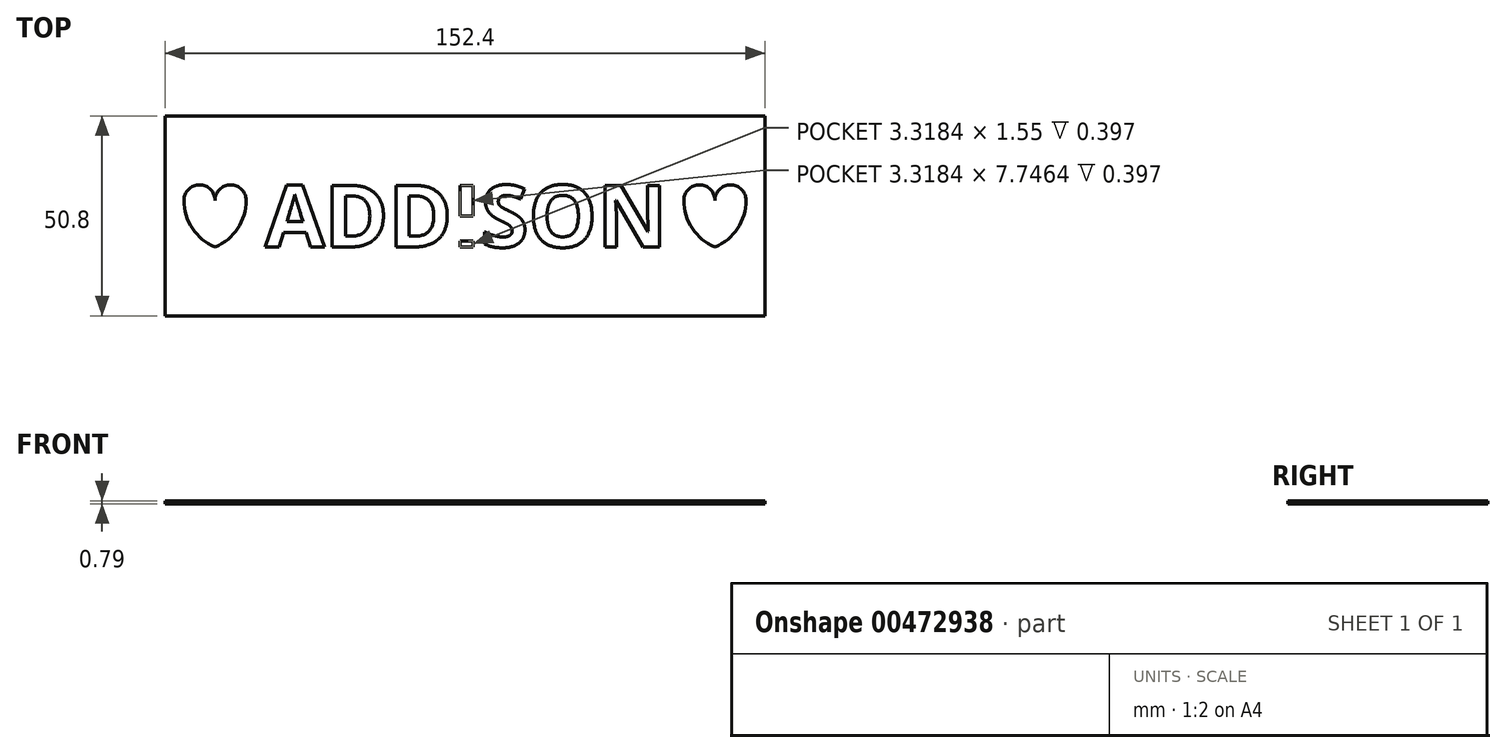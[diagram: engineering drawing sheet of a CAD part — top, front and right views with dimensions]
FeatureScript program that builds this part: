
annotation { "Feature Type Name" : "Feature", "Feature Type Description" : "" }
export const myFeature = defineFeature(function(context is Context, id is Id, definition is map)
    precondition{}
    {
        {
            var Q0;
            Q0=qCreatedBy(makeId("Top.planeOp"),FACE);
            var sketch = newSketch(context, id + "F0", { "sketchPlane" : qUnion([Q0])});
            skLineSegment(sketch, "E0", {"start": v(0, 0) * mm, "end": v(0, 25.4) * mm});
            skLineSegment(sketch, "E1", {"start": v(0, 25.4) * mm, "end": v(-76.2, 25.4) * mm});
            skLineSegment(sketch, "E2", {"start": v(-76.2, 25.4) * mm, "end": v(-76.2, -25.4) * mm});
            skLineSegment(sketch, "E3", {"start": v(-76.2, -25.4) * mm, "end": v(76.2, -25.4) * mm});
            skLineSegment(sketch, "E4", {"start": v(76.2, -25.4) * mm, "end": v(76.2, 25.4) * mm});
            skLineSegment(sketch, "E5", {"start": v(76.2, 25.4) * mm, "end": v(0, 25.4) * mm});
            skSolve(sketch);
        }
        {
            var Q0;
            Q0 = qSketchRegion(id + "F0", true);
            extrude(context, id + "F1", {"entities" : qUnion([Q0]), "depth" : 0.8 * mm, "offsetDistance" : 25.4 * mm});
        }
        {
            var Q0;
            Q0=makeQuery(id+"F1.opExtrude","CAP_FACE",FACE,{"disambiguationData":[OSD([sQuery(id+"F0.wireOp",EDGE,"E1"),sQuery(id+"F0.wireOp",EDGE,"E2"),sQuery(id+"F0.wireOp",EDGE,"E3"),sQuery(id+"F0.wireOp",EDGE,"E4"),sQuery(id+"F0.wireOp",EDGE,"E5")])],"isStart":false});
            var sketch = newSketch(context, id + "F2", { "sketchPlane" : qUnion([Q0])});
            skLineSegment(sketch, "E6.top", {"start": v(-44.45, -6.35) * mm, "end": v(44.45, -6.35) * mm});
            skPoint(sketch, "E6.middle", {"position": v(0, 0) * mm});
            skText(sketch, "E7", { "text": "ADDISON", "fontName": "OpenSans-Bold.ttf"});
            skLineSegment(sketch, "E8", {"start": v(0, 0) * mm, "end": v(-63.5, 0) * mm});
            skPoint(sketch, "E8.endSnap0", {"position": v(-76.2, 0) * mm});
            skLineSegment(sketch, "E9", {"start": v(-63.5, 0) * mm, "end": v(63.5, 0) * mm});
            skLineSegment(sketch, "E10", {"start": v(-63.5, 0) * mm, "end": v(-63.5, -7.9) * mm});
            skLineSegment(sketch, "E11", {"start": v(-63.5, 0) * mm, "end": v(-63.5, 3.94) * mm});
            skLineSegment(sketch, "E12", {"start": v(-63.5, 3.94) * mm, "end": v(-59.56, 3.94) * mm});
            skLineSegment(sketch, "E13", {"start": v(-63.5, 3.94) * mm, "end": v(-67.44, 3.94) * mm});
            skArc(sketch, "E14", {"start": v(-55.61, 3.94) * mm, "mid": v(-59.56, 7.89) * mm, "end": v(-63.5, 3.94) * mm});
            skArc(sketch, "E15", {"start": v(-63.5, 3.94) * mm, "mid": v(-67.44, 7.89) * mm, "end": v(-71.39, 3.94) * mm});
            skArc(sketch, "E16", {"start": v(-63.5, -7.9) * mm, "mid": v(-57.74, -3.18) * mm, "end": v(-55.61, 3.94) * mm});
            skArc(sketch, "E17", {"start": v(-71.39, 3.94) * mm, "mid": v(-69.26, -3.18) * mm, "end": v(-63.5, -7.9) * mm});
            skLineSegment(sketch, "E18", {"start": v(63.5, 0) * mm, "end": v(63.5, -7.9) * mm});
            skLineSegment(sketch, "E19", {"start": v(63.5, 0) * mm, "end": v(63.5, 3.94) * mm});
            skLineSegment(sketch, "E20", {"start": v(63.5, 3.94) * mm, "end": v(59.56, 3.94) * mm});
            skLineSegment(sketch, "E21", {"start": v(63.5, 3.94) * mm, "end": v(67.44, 3.94) * mm});
            skArc(sketch, "E22", {"start": v(63.5, 3.94) * mm, "mid": v(59.56, 7.89) * mm, "end": v(55.61, 3.94) * mm});
            skArc(sketch, "E23", {"start": v(71.39, 3.94) * mm, "mid": v(67.44, 7.89) * mm, "end": v(63.5, 3.94) * mm});
            skArc(sketch, "E24", {"start": v(63.5, -7.9) * mm, "mid": v(69.26, -3.18) * mm, "end": v(71.39, 3.94) * mm});
            skArc(sketch, "E25", {"start": v(55.61, 3.94) * mm, "mid": v(57.74, -3.18) * mm, "end": v(63.5, -7.9) * mm});
            const initialGuessF2  = {"E7": [-0.0508, -0.0079, 1, 0, 0.01578]};
            skSetInitialGuess(sketch, initialGuessF2);
            skSolve(sketch);
        }
        {
            var Q0;
            {var subQ6=sQuery(id+"F2.wireOp",EDGE,"E7.sketch_text.stroke-84");Q0=makeQuery(id+"F2.imprint","IMPRINT",FACE,{"disambiguationData":[TD([[makeQuery(id+"F2.imprint","IMPRINT",EDGE,{"derivedFrom":subQ6}),-1.0]])]});}
            var Q1;
            {var subQ4=sQuery(id+"F2.wireOp",EDGE,"E7.sketch_text.stroke-82");Q1=makeQuery(id+"F2.imprint","IMPRINT",FACE,{"disambiguationData":[TD([[makeQuery(id+"F2.imprint","IMPRINT",EDGE,{"derivedFrom":subQ4}),-1.0]])]});}
            var Q2;
            {var subQ4=sQuery(id+"F2.wireOp",EDGE,"E7.sketch_text.stroke-93");Q2=makeQuery(id+"F2.imprint","IMPRINT",FACE,{"disambiguationData":[TD([[makeQuery(id+"F2.imprint","IMPRINT",EDGE,{"derivedFrom":subQ4}),-1.0]])]});}
            var Q3;
            {var subQ3=sQuery(id+"F2.wireOp",EDGE,"E6.top");var subQ5=sQuery(id+"F2.wireOp",EDGE,"E7.sketch_text.stroke-88");var subQ6=makeQuery(id+"F2.imprint","INTERSECT",VERTEX,{"derivedFrom":[subQ3,subQ5]});Q3=makeQuery(id+"F2.imprint","IMPRINT",FACE,{"disambiguationData":[TD([[makeQuery(id+"F2.imprint","IMPRINT",EDGE,{"disambiguationData":[TD([[subQ6,-1.0]])],"derivedFrom":subQ3}),1.0]])]});}
            var Q4;
            {var subQ5=sQuery(id+"F2.wireOp",EDGE,"E7.sketch_text.stroke-87");Q4=makeQuery(id+"F2.imprint","IMPRINT",FACE,{"disambiguationData":[TD([[makeQuery(id+"F2.imprint","IMPRINT",EDGE,{"derivedFrom":subQ5}),-1.0]])]});}
            var Q5;
            {var subQ6=sQuery(id+"F2.wireOp",EDGE,"E7.sketch_text.stroke-68");Q5=makeQuery(id+"F2.imprint","IMPRINT",FACE,{"disambiguationData":[TD([[makeQuery(id+"F2.imprint","IMPRINT",EDGE,{"derivedFrom":subQ6}),-1.0]])]});}
            var Q6;
            {var subQ4=sQuery(id+"F2.wireOp",EDGE,"E7.sketch_text.stroke-73");Q6=makeQuery(id+"F2.imprint","IMPRINT",FACE,{"disambiguationData":[TD([[makeQuery(id+"F2.imprint","IMPRINT",EDGE,{"derivedFrom":subQ4}),-1.0]])]});}
            var Q7;
            {var subQ0=sQuery(id+"F2.wireOp",EDGE,"E7.sketch_text.stroke-70");var subQ1=sQuery(id+"F2.wireOp",EDGE,"E6.top");var subQ2=makeQuery(id+"F2.imprint","INTERSECT",VERTEX,{"derivedFrom":[subQ1,subQ0]});Q7=makeQuery(id+"F2.imprint","IMPRINT",FACE,{"disambiguationData":[TD([[makeQuery(id+"F2.imprint","IMPRINT",EDGE,{"disambiguationData":[TD([[subQ2,-1.0]])],"derivedFrom":subQ1}),-1.0]])]});}
            var Q8;
            {var subQ10=sQuery(id+"F2.wireOp",EDGE,"E7.sketch_text.stroke-44");Q8=makeQuery(id+"F2.imprint","IMPRINT",FACE,{"disambiguationData":[TD([[makeQuery(id+"F2.imprint","IMPRINT",EDGE,{"derivedFrom":subQ10}),-1.0]])]});}
            var Q9;
            {var subQ5=sQuery(id+"F2.wireOp",EDGE,"E7.sketch_text.stroke-52");Q9=makeQuery(id+"F2.imprint","IMPRINT",FACE,{"disambiguationData":[TD([[makeQuery(id+"F2.imprint","IMPRINT",EDGE,{"derivedFrom":subQ5}),-1.0]])]});}
            var Q10;
            {var subQ1=sQuery(id+"F2.wireOp",EDGE,"E7.sketch_text.stroke-41");Q10=makeQuery(id+"F2.imprint","IMPRINT",FACE,{"disambiguationData":[TD([[makeQuery(id+"F2.imprint","IMPRINT",EDGE,{"derivedFrom":subQ1}),-1.0]])]});}
            var Q11;
            {var subQ5=sQuery(id+"F2.wireOp",EDGE,"E7.sketch_text.stroke-39");Q11=makeQuery(id+"F2.imprint","IMPRINT",FACE,{"disambiguationData":[TD([[makeQuery(id+"F2.imprint","IMPRINT",EDGE,{"derivedFrom":subQ5}),-1.0]])]});}
            var Q12;
            {var subQ3=sQuery(id+"F2.wireOp",EDGE,"E9");var subQ5=makeQuery(id+"F2.imprint","IMPRINT",VERTEX,{"derivedFrom":subQ3});Q12=makeQuery(id+"F2.imprint","IMPRINT",FACE,{"disambiguationData":[TD([[makeQuery(id+"F2.imprint","IMPRINT",EDGE,{"disambiguationData":[TD([[subQ5,1.0]])],"derivedFrom":subQ3}),-1.0]])]});}
            var Q13;
            {var subQ5=sQuery(id+"F2.wireOp",EDGE,"E7.sketch_text.stroke-37");Q13=makeQuery(id+"F2.imprint","IMPRINT",FACE,{"disambiguationData":[TD([[makeQuery(id+"F2.imprint","IMPRINT",EDGE,{"derivedFrom":subQ5}),-1.0]])]});}
            var Q14;
            {var subQ0=sQuery(id+"F2.wireOp",EDGE,"E7.sketch_text.stroke-28");Q14=makeQuery(id+"F2.imprint","IMPRINT",FACE,{"disambiguationData":[TD([[makeQuery(id+"F2.imprint","IMPRINT",EDGE,{"derivedFrom":subQ0}),-1.0]])]});}
            var Q15;
            {var subQ15=sQuery(id+"F2.wireOp",EDGE,"E7.sketch_text.stroke-34");Q15=makeQuery(id+"F2.imprint","IMPRINT",FACE,{"disambiguationData":[TD([[makeQuery(id+"F2.imprint","IMPRINT",EDGE,{"derivedFrom":subQ15}),-1.0]])]});}
            var Q16;
            {var subQ5=sQuery(id+"F2.wireOp",EDGE,"E7.sketch_text.stroke-26");Q16=makeQuery(id+"F2.imprint","IMPRINT",FACE,{"disambiguationData":[TD([[makeQuery(id+"F2.imprint","IMPRINT",EDGE,{"derivedFrom":subQ5}),-1.0]])]});}
            var Q17;
            {var subQ15=sQuery(id+"F2.wireOp",EDGE,"E7.sketch_text.stroke-22");Q17=makeQuery(id+"F2.imprint","IMPRINT",FACE,{"disambiguationData":[TD([[makeQuery(id+"F2.imprint","IMPRINT",EDGE,{"derivedFrom":subQ15}),-1.0]])]});}
            var Q18;
            {var subQ0=sQuery(id+"F2.wireOp",EDGE,"E7.sketch_text.stroke-16");Q18=makeQuery(id+"F2.imprint","IMPRINT",FACE,{"disambiguationData":[TD([[makeQuery(id+"F2.imprint","IMPRINT",EDGE,{"derivedFrom":subQ0}),-1.0]])]});}
            var Q19;
            {var subQ5=sQuery(id+"F2.wireOp",EDGE,"E7.sketch_text.stroke-14");Q19=makeQuery(id+"F2.imprint","IMPRINT",FACE,{"disambiguationData":[TD([[makeQuery(id+"F2.imprint","IMPRINT",EDGE,{"derivedFrom":subQ5}),-1.0]])]});}
            var Q20;
            {var subQ5=sQuery(id+"F2.wireOp",EDGE,"E7.sketch_text.stroke-7");Q20=makeQuery(id+"F2.imprint","IMPRINT",FACE,{"disambiguationData":[TD([[makeQuery(id+"F2.imprint","IMPRINT",EDGE,{"derivedFrom":subQ5}),-1.0]])]});}
            var Q21;
            {var subQ15=sQuery(id+"F2.wireOp",EDGE,"E7.sketch_text.stroke-1");Q21=makeQuery(id+"F2.imprint","IMPRINT",FACE,{"disambiguationData":[TD([[makeQuery(id+"F2.imprint","IMPRINT",EDGE,{"derivedFrom":subQ15}),-1.0]])]});}
            var Q22;
            {var subQ5=sQuery(id+"F2.wireOp",EDGE,"E7.sketch_text.stroke-5");Q22=makeQuery(id+"F2.imprint","IMPRINT",FACE,{"disambiguationData":[TD([[makeQuery(id+"F2.imprint","IMPRINT",EDGE,{"derivedFrom":subQ5}),-1.0]])]});}
            var Q23;
            {var subQ0=sQuery(id+"F2.wireOp",EDGE,"E11");Q23=makeQuery(id+"F2.imprint","IMPRINT",FACE,{"disambiguationData":[TD([[makeQuery(id+"F2.imprint","IMPRINT",EDGE,{"derivedFrom":subQ0}),-1.0]])]});}
            var Q24;
            Q24=makeQuery(id+"F2.imprint","IMPRINT",FACE,{"disambiguationData":[TD([[makeQuery(id+"F2.imprint","IMPRINT",EDGE,{"derivedFrom":sQuery(id+"F2.wireOp",EDGE,"E10")}),-1.0]])]});
            var Q25;
            {var subQ0=sQuery(id+"F2.wireOp",EDGE,"E10");Q25=makeQuery(id+"F2.imprint","IMPRINT",FACE,{"disambiguationData":[TD([[makeQuery(id+"F2.imprint","IMPRINT",EDGE,{"derivedFrom":subQ0}),1.0]])]});}
            var Q26;
            {var subQ0=sQuery(id+"F2.wireOp",EDGE,"E19");Q26=makeQuery(id+"F2.imprint","IMPRINT",FACE,{"disambiguationData":[TD([[makeQuery(id+"F2.imprint","IMPRINT",EDGE,{"derivedFrom":subQ0}),1.0]])]});}
            var Q27;
            Q27=makeQuery(id+"F2.imprint","IMPRINT",FACE,{"disambiguationData":[TD([[makeQuery(id+"F2.imprint","IMPRINT",EDGE,{"derivedFrom":sQuery(id+"F2.wireOp",EDGE,"E18")}),1.0]])]});
            var Q28;
            {var subQ0=sQuery(id+"F2.wireOp",EDGE,"E18");Q28=makeQuery(id+"F2.imprint","IMPRINT",FACE,{"disambiguationData":[TD([[makeQuery(id+"F2.imprint","IMPRINT",EDGE,{"derivedFrom":subQ0}),-1.0]])]});}
            extrude(context, id + "F3", {"entities" : qUnion([Q0, Q1, Q2, Q3, Q4, Q5, Q6, Q7, Q8, Q9, Q10, Q11, Q12, Q13, Q14, Q15, Q16, Q17, Q18, Q19, Q20, Q21, Q22, Q23, Q24, Q25, Q26, Q27, Q28]), "operationType" : NewBodyOperationType.REMOVE, "oppositeDirection" : true, "depth" : 0.4 * mm, "offsetDistance" : 25.4 * mm});
        }
    });
